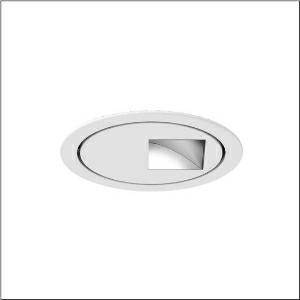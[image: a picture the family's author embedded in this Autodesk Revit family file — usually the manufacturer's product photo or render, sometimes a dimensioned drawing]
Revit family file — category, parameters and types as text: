
# Revit family: lunis_11_mini_round_51dk11cd2wg21
name_source: partatom
category: Lighting Fixtures
units: mm (PartAtom-declared; Revit-internal decimal feet)

## family parameters
Cut with Voids When Loaded = No
Host = Face
Light Source = No
Part Type = Normal
Room Calculation Point = No
Round Connector Dimension = Use Diameter
Shared = No

## types (1)
- Lunis 11 mini round (1 x LED 4000K / CRI = 80 (unbekannt), 2470 lm, 4000K)
    Apparent Load = 28 VA
    CIE Flux Codes = 44 77 97 100 100
    Color Rendering = 80
    Color Temperature = 4000K
    Default Elevation = 1800 mm
    Description = Lunis 11 mini round, downlight, light control with wallwasher, of highly reflective aluminium, highly specular, light emission: direct distribution, LED rated luminous flux: 2.470lm, light colour: 840, control gear: ECG, with terminal, 5-pole, mains connection: 220..230V, AC/DC, 0/50..60Hz, LED module, luminaire module, of aluminium, highly specular, white, diameter: 176mm, clamping range: 1..40mm, recessing ring, of plastic, traffic white (RAL 9016), protection rating (complete): IP20, insulation class (complete): insulation class II (safety insulation), certification: CE, permissible ambient temperature for indoor applications: 0..+35°C, packaging unit: 1 piece
    Height = 0 mm  [stored 0 ft]
    Lamp = 1 x LED 4000K / CRI >= 80 (unbekannt)
    Lamp Light Flux = 2470 lm
    Lamp count = 1
    Length = 176 mm
    Luminous efficacy = 89 lm/W
    Manufacturer = Siteco
    ModVariant = No
    Model = 51DK11CD2WG21
    Mounting Place = Ceiling
    Mounting Type = Recessed
    Number of Poles = 1
    OnlyDefault = Yes
    Power Factor = 1
    Product Name = Lunis 11 mini round
    Product group = downlight
    ProductGroupID = 401
    Protection Class = Protection class II
    Protection Degree = IP 20
    RLX_Detail_Level = 1
    RLX_Emergency_Light_Flux = 0 lm
    RLX_Emergency_Type = 0
    RLX_Emergency_Type_DB = No
    RlxData = <blob elided: 59317 chars, md5=f3adb3d3>
    Socket = socket
    Standby Power = 0 W
    System Light Flux = 2470 lm
    System Power = 28 W
    Type Comments = Product without accessories
    Type Image = l_1004772.jpg
    URL = http://relux.com
    VarID = ---
    Voltage = 0 V
    Weight = 0.00 kg
    Width = 176 mm

note: [stored X ft] marks values corroborated as IEEE doubles in the binary element streams (Revit-internal decimal feet)

## geometry (parser evidence)
native form markers: Blend x4, Sweep x8
no freeform markers — native parametric forms only
